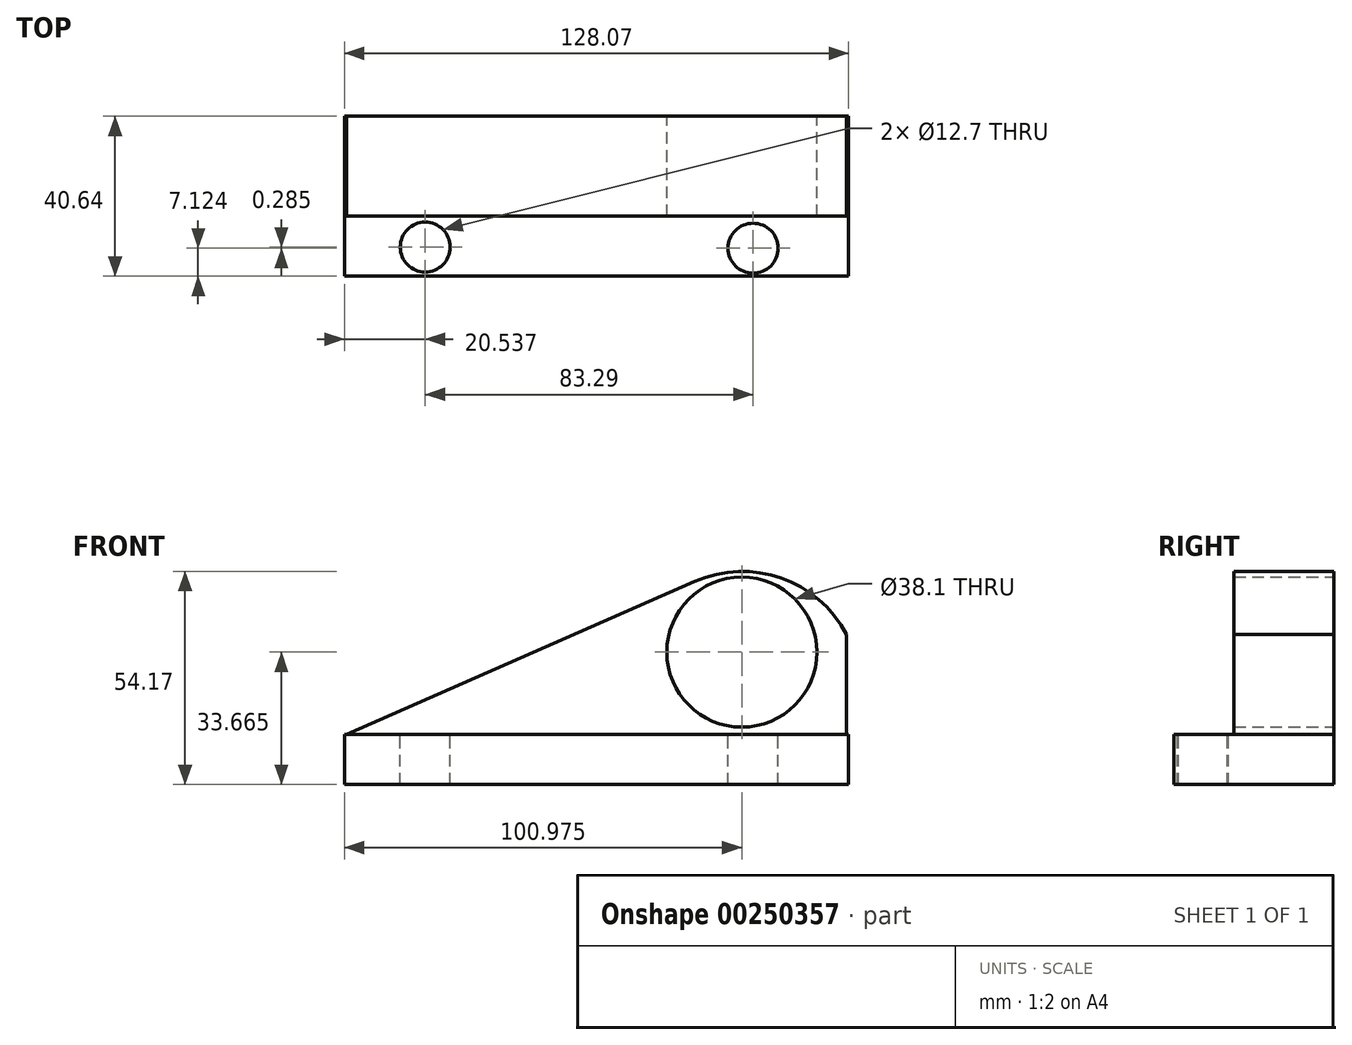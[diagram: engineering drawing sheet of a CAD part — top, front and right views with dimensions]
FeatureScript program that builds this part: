
annotation { "Feature Type Name" : "Feature", "Feature Type Description" : "" }
export const myFeature = defineFeature(function(context is Context, id is Id, definition is map)
    precondition{}
    {
        {
            var Q0;
            Q0=qCreatedBy(makeId("Front.planeOp"),FACE);
            var sketch = newSketch(context, id + "F0", { "sketchPlane" : qUnion([Q0])});
            skLineSegment(sketch, "E0", {"start": v(-70.74, 0) * mm, "end": v(56.26, 0) * mm});
            skLineSegment(sketch, "E1", {"start": v(-70.74, 0) * mm, "end": v(17.68, 38.94) * mm});
            skLineSegment(sketch, "E2", {"start": v(56.26, 0) * mm, "end": v(56.26, 25.4) * mm});
            skArc(sketch, "E3", {"start": v(56.26, 25.4) * mm, "mid": v(39.65, 39.78) * mm, "end": v(17.68, 38.94) * mm});
            skSolve(sketch);
        }
        {
            var Q0;
            Q0=qCreatedBy(makeId("Front.planeOp"),FACE);
            var sketch = newSketch(context, id + "F1", { "sketchPlane" : qUnion([Q0])});
            skPoint(sketch, "E4.start.orphan", {"position": v(-71.31, 0) * mm});
            skLineSegment(sketch, "E5", {"start": v(-71.31, 0) * mm, "end": v(-71.31, -12.7) * mm});
            skLineSegment(sketch, "E6", {"start": v(56.76, -12.7) * mm, "end": v(56.76, 0) * mm});
            skLineSegment(sketch, "E7", {"start": v(56.76, 0) * mm, "end": v(56.76, -12.7) * mm});
            skLineSegment(sketch, "E8", {"start": v(56.76, -12.7) * mm, "end": v(-71.31, -12.7) * mm});
            skLineSegment(sketch, "E9", {"start": v(-71.31, 0) * mm, "end": v(56.76, 0) * mm});
            skSolve(sketch);
        }
        {
            var Q0;
            Q0=makeQuery(id+"F0.imprint","IMPRINT",FACE,{"disambiguationData":[TD([[makeQuery(id+"F0.imprint","IMPRINT",EDGE,{"derivedFrom":sQuery(id+"F0.wireOp",EDGE,"E0")}),1.0]])]});
            extrude(context, id + "F2", {"entities" : qUnion([Q0]), "depth" : 25.4 * mm});
        }
        {
            var Q0;
            Q0=makeQuery(id+"F1.imprint","IMPRINT",FACE,{"disambiguationData":[TD([[makeQuery(id+"F1.imprint","IMPRINT",EDGE,{"derivedFrom":sQuery(id+"F1.wireOp",EDGE,"E5")}),1.0]])]});
            extrude(context, id + "F3", {"entities" : qUnion([Q0]), "operationType" : NewBodyOperationType.ADD, "depth" : 40.64 * mm});
        }
        {
            var Q0;
            Q0=qCreatedBy(makeId("Front.planeOp"),FACE);
            var sketch = newSketch(context, id + "F4", { "sketchPlane" : qUnion([Q0])});
            skLineSegment(sketch, "E10", {"start": v(29.67, 20.97) * mm, "end": v(5.42, 20.97) * mm});
            skSolve(sketch);
        }
        {
            var Q0;
            Q0=sQuery(id+"F4.wireOp",VERTEX,"E10.start");
            var Q1;
            Q1=makeQuery(id+"F2.opExtrude","SWEPT_BODY",BODY,{"disambiguationData":[OSD([sQuery(id+"F0.wireOp",EDGE,"E0"),sQuery(id+"F0.wireOp",EDGE,"E1"),sQuery(id+"F0.wireOp",EDGE,"E2"),sQuery(id+"F0.wireOp",EDGE,"E3")])]});
            hole(context, id + "F5", {"style" : HoleStyle.SIMPLE, "endStyle" : HoleEndStyle.THROUGH, "oppositeDirection" : true, "holeDiameter" : 38.1 * mm, "tappedDepth" : 12.7 * mm, "tapClearance" : 3, "locations" : qUnion([Q0]), "scope" : qUnion([Q1])});
        }
        {
            var Q0;
            Q0=qCreatedBy(makeId("Top.planeOp"),FACE);
            var sketch = newSketch(context, id + "F6", { "sketchPlane" : qUnion([Q0])});
            skLineSegment(sketch, "E11", {"start": v(-50.77, -33.23) * mm, "end": v(-63.04, -33.23) * mm});
            skSolve(sketch);
        }
        {
            var Q0;
            Q0=sQuery(id+"F6.wireOp",VERTEX,"E11.start");
            var Q1;
            Q1=makeQuery(id+"F2.opExtrude","SWEPT_BODY",BODY,{"disambiguationData":[OSD([sQuery(id+"F0.wireOp",EDGE,"E0"),sQuery(id+"F0.wireOp",EDGE,"E1"),sQuery(id+"F0.wireOp",EDGE,"E2"),sQuery(id+"F0.wireOp",EDGE,"E3")])]});
            hole(context, id + "F7", {"style" : HoleStyle.SIMPLE, "endStyle" : HoleEndStyle.THROUGH, "holeDiameter" : 12.7 * mm, "tappedDepth" : 12.7 * mm, "tapClearance" : 3, "locations" : qUnion([Q0]), "scope" : qUnion([Q1])});
        }
        {
            var Q0;
            Q0=qCreatedBy(makeId("Top.planeOp"),FACE);
            var sketch = newSketch(context, id + "F8", { "sketchPlane" : qUnion([Q0])});
            skLineSegment(sketch, "E12", {"start": v(32.52, -33.52) * mm, "end": v(21.1, -33.52) * mm});
            skSolve(sketch);
        }
        {
            var Q0;
            Q0=sQuery(id+"F8.wireOp",VERTEX,"E12.start");
            var Q1;
            Q1=makeQuery(id+"F2.opExtrude","SWEPT_BODY",BODY,{"disambiguationData":[OSD([sQuery(id+"F0.wireOp",EDGE,"E0"),sQuery(id+"F0.wireOp",EDGE,"E1"),sQuery(id+"F0.wireOp",EDGE,"E2"),sQuery(id+"F0.wireOp",EDGE,"E3")])]});
            hole(context, id + "F9", {"style" : HoleStyle.SIMPLE, "endStyle" : HoleEndStyle.THROUGH, "holeDiameter" : 12.7 * mm, "tappedDepth" : 12.7 * mm, "tapClearance" : 3, "locations" : qUnion([Q0]), "scope" : qUnion([Q1])});
        }
    });
